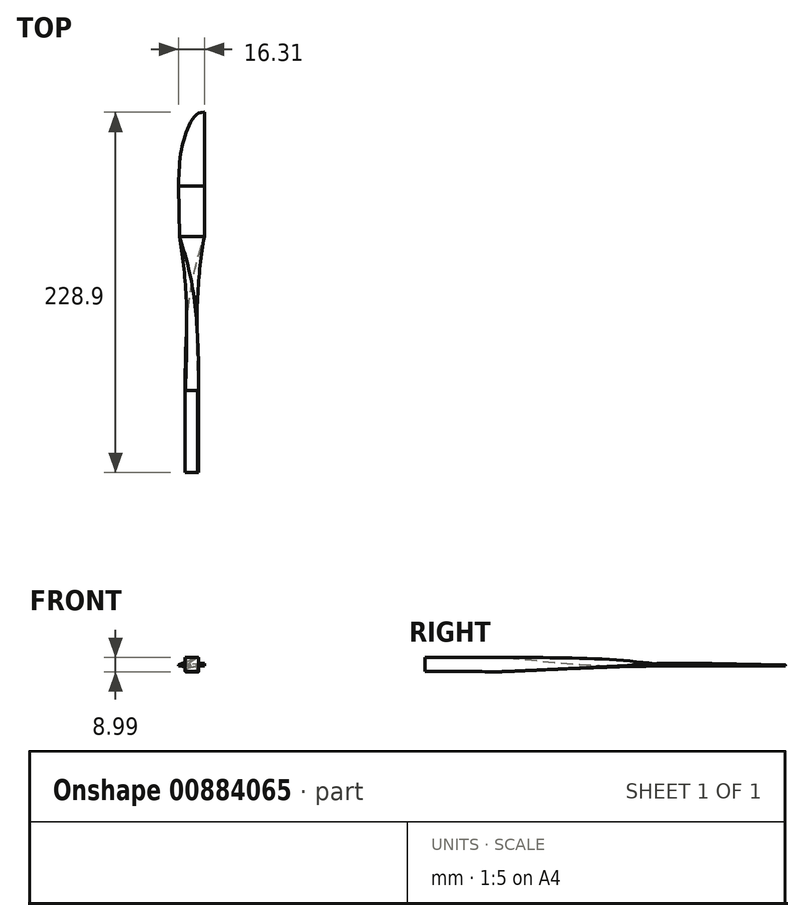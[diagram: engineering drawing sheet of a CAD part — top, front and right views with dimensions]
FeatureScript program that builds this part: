
annotation { "Feature Type Name" : "Feature", "Feature Type Description" : "" }
export const myFeature = defineFeature(function(context is Context, id is Id, definition is map)
    precondition{}
    {
        {
            var Q0;
            Q0=qCreatedBy(makeId("Front.planeOp"),FACE);
            var sketch = newSketch(context, id + "F0", { "sketchPlane" : qUnion([Q0])});
            skLineSegment(sketch, "E0.bottom", {"start": v(4.2, 4.4) * mm, "end": v(-4.2, 4.4) * mm});
            skLineSegment(sketch, "E0.top", {"start": v(4.2, -4.4) * mm, "end": v(-4.2, -4.4) * mm});
            skLineSegment(sketch, "E0.left", {"start": v(4.2, 4.4) * mm, "end": v(4.2, -4.4) * mm});
            skLineSegment(sketch, "E0.right", {"start": v(-4.2, 4.4) * mm, "end": v(-4.2, -4.4) * mm});
            skPoint(sketch, "E0.middle", {"position": v(0, 0) * mm});
            skSolve(sketch);
        }
        {
            var Q0;
            Q0=qCreatedBy(makeId("Front.planeOp"),FACE);
            cPlane(context, id + "F1", {"entities" : qUnion([Q0]), "cplaneType" : CPlaneType.OFFSET, "offset" : 120 * mm, "oppositeDirection" : true, "width" : 150 * mm, "height" : 150 * mm});
        }
        {
            var Q0;
            Q0=qCreatedBy(makeId("Front.planeOp"),FACE);
            cPlane(context, id + "F2", {"entities" : qUnion([Q0]), "cplaneType" : CPlaneType.OFFSET, "offset" : 52 * mm, "oppositeDirection" : true, "width" : 150 * mm, "height" : 150 * mm});
        }
        {
            var Q0;
            Q0=qCreatedBy(id+"F2.planeOp",FACE);
            var sketch = newSketch(context, id + "F3", { "sketchPlane" : qUnion([Q0])});
            skLineSegment(sketch, "E1.0.0", {"start": v(-4.2, -4.4) * mm, "end": v(4.2, -4.4) * mm});
            skLineSegment(sketch, "E1.0.1", {"start": v(4.2, -4.4) * mm, "end": v(4.2, 4.4) * mm});
            skLineSegment(sketch, "E1.0.2", {"start": v(4.2, 4.4) * mm, "end": v(-4.2, 4.4) * mm});
            skLineSegment(sketch, "E1.0.3", {"start": v(-4.2, 4.4) * mm, "end": v(-4.2, -4.4) * mm});
            skSolve(sketch);
        }
        {
            var Q0;
            Q0=sQuery(id+"F0.wireOp",VERTEX,"E0.bottom.end");
            var Q1;
            Q1=sQuery(id+"F3.wireOp",VERTEX,"E1.0.2.end");
            var Q2;
            Q2=sQuery(id+"F3.wireOp",VERTEX,"E1.0.1.end");
            cPlane(context, id + "F4", {"entities" : qUnion([Q0, Q1, Q2]), "cplaneType" : CPlaneType.THREE_POINT, "offset" : 25 * mm, "width" : 150 * mm, "height" : 150 * mm});
        }
        {
            var Q0;
            Q0=qCreatedBy(id+"F4.planeOp",FACE);
            var sketch = newSketch(context, id + "F5", { "sketchPlane" : qUnion([Q0])});
            skLineSegment(sketch, "E2", {"start": v(-12.8, 0) * mm, "end": v(-12.8, 52) * mm});
            skLineSegment(sketch, "E3", {"start": v(4.2, 0) * mm, "end": v(4.2, 52) * mm});
            skLineSegment(sketch, "E4.0", {"start": v(4.2, 52) * mm, "end": v(-12.8, 52) * mm});
            skLineSegment(sketch, "E5.0", {"start": v(4.2, 0) * mm, "end": v(-12.8, 0) * mm});
            skPoint(sketch, "E6.orphan", {"position": v(-4.2, 52) * mm});
            skPoint(sketch, "E7.orphan", {"position": v(-4.2, 0) * mm});
            skSolve(sketch);
        }
        {
            var Q0;
            Q0=qCreatedBy(id+"F1.planeOp",FACE);
            var sketch = newSketch(context, id + "F6", { "sketchPlane" : qUnion([Q0])});
            skLineSegment(sketch, "E8", {"start": v(-4.15, -1) * mm, "end": v(4.15, -1) * mm, "construction": true});
            skPoint(sketch, "E9", {"position": v(0, -1) * mm});
            skPoint(sketch, "E10", {"position": v(0, 3) * mm});
            skLineSegment(sketch, "E11", {"start": v(4.15, -1) * mm, "end": v(0, 3) * mm});
            skLineSegment(sketch, "E12", {"start": v(-4.15, -1) * mm, "end": v(0, 3) * mm});
            skLineSegment(sketch, "E13", {"start": v(-4.15, -1) * mm, "end": v(0, -1.5) * mm});
            skLineSegment(sketch, "E14", {"start": v(0, -1.5) * mm, "end": v(4.15, -1) * mm});
            skSolve(sketch);
        }
        {
            var Q0;
            Q0=qCreatedBy(id+"F1.planeOp",FACE);
            cPlane(context, id + "F7", {"entities" : qUnion([Q0]), "cplaneType" : CPlaneType.OFFSET, "offset" : 30 * mm, "oppositeDirection" : true, "width" : 150 * mm, "height" : 150 * mm});
        }
        {
            var Q0;
            Q0=qCreatedBy(id+"F7.planeOp",FACE);
            var sketch = newSketch(context, id + "F8", { "sketchPlane" : qUnion([Q0])});
            skLineSegment(sketch, "E15.bottom", {"start": v(-7.87, -0.75) * mm, "end": v(7.87, -0.75) * mm});
            skLineSegment(sketch, "E15.top", {"start": v(-7.88, 0.05) * mm, "end": v(7.87, 0.75) * mm});
            skLineSegment(sketch, "E15.left", {"start": v(-7.87, -0.75) * mm, "end": v(-7.87, 0.05) * mm});
            skLineSegment(sketch, "E15.right", {"start": v(7.87, -0.75) * mm, "end": v(7.87, 0.75) * mm});
            skPoint(sketch, "E16", {"position": v(0, -0.75) * mm});
            skSolve(sketch);
        }
        {
            var Q0;
            Q0=makeQuery(id+"F0.imprint","IMPRINT",FACE,{"disambiguationData":[TD([[makeQuery(id+"F0.imprint","IMPRINT",EDGE,{"derivedFrom":sQuery(id+"F0.wireOp",EDGE,"E0.bottom")}),1.0]])]});
            var Q1;
            Q1=makeQuery(id+"F3.imprint","IMPRINT",FACE,{"disambiguationData":[TD([[makeQuery(id+"F3.imprint","IMPRINT",EDGE,{"derivedFrom":sQuery(id+"F3.wireOp",EDGE,"E1.0.0")}),1.0]])]});
            var Q2;
            Q2 = qSketchRegion(id + "F6", true);
            var Q3;
            Q3 = qSketchRegion(id + "F8", true);
            var Q4;
            Q4=sQuery(id+"F5.wireOp",EDGE,"E2");
            var Q5;
            Q5=sQuery(id+"F5.wireOp",EDGE,"E3");
            var Q6;
            Q6=sQuery(id+"F0.wireOp",VERTEX,"E0.bottom.start");
            var Q7;
            Q7=sQuery(id+"F3.wireOp",VERTEX,"E1.0.1.end");
            var Q8;
            Q8=sQuery(id+"F6.wireOp",VERTEX,"E10");
            var Q9;
            Q9=sQuery(id+"F8.wireOp",VERTEX,"E15.top.start");
            loft(context, id + "F9", {"startCondition" : LoftEndDerivativeType.NORMAL_TO_PROFILE, "startMagnitude" : 2.75, "sheetProfilesArray" : [{ "sheetProfileEntities" : qUnion([Q0]) }, { "sheetProfileEntities" : qUnion([Q1]) }, { "sheetProfileEntities" : qUnion([Q2]) }, { "sheetProfileEntities" : qUnion([Q3]) }], "guidesArray" : [{ "guideEntities" : qUnion([Q4]), "guideDerivativeType" : LoftGuideDerivativeType.DEFAULT, "guideDerivativeMagnitude" : 1 }, { "guideEntities" : qUnion([Q5]), "guideDerivativeType" : LoftGuideDerivativeType.DEFAULT, "guideDerivativeMagnitude" : 1 }], "matchConnections" : true, "connections" : [{ "connectionEntities" : qUnion([Q6, Q7, Q8, Q9]), "connectionEdgeQueries" : qUnion([]), "connectionEdgeParameters" : [] }]});
        }
        {
            var Q0;
            Q0 = qSketchRegion(id + "F5", true);
            extrude(context, id + "F10", {"entities" : qUnion([Q0]), "operationType" : NewBodyOperationType.REMOVE, "endBound" : BoundingType.THROUGH_ALL, "depth" : 25 * mm, "offsetDistance" : 25 * mm});
        }
        {
            var Q0;
            Q0=qCreatedBy(id+"F7.planeOp",FACE);
            cPlane(context, id + "F11", {"entities" : qUnion([Q0]), "cplaneType" : CPlaneType.OFFSET, "offset" : 32 * mm, "oppositeDirection" : true, "width" : 150 * mm, "height" : 150 * mm});
        }
        {
            var Q0;
            Q0=qCreatedBy(id+"F11.planeOp",FACE);
            cPlane(context, id + "F12", {"entities" : qUnion([Q0]), "cplaneType" : CPlaneType.OFFSET, "offset" : 46.9 * mm, "oppositeDirection" : true, "width" : 150 * mm, "height" : 150 * mm});
        }
        {
            var Q0;
            Q0=qCreatedBy(id+"F11.planeOp",FACE);
            var sketch = newSketch(context, id + "F13", { "sketchPlane" : qUnion([Q0])});
            skLineSegment(sketch, "E17", {"start": v(7.87, -0.75) * mm, "end": v(-8.43, -0.75) * mm});
            skLineSegment(sketch, "E18", {"start": v(7.87, -0.75) * mm, "end": v(7.87, 0.65) * mm});
            skLineSegment(sketch, "E19", {"start": v(7.87, 0.65) * mm, "end": v(-8.43, -0.35) * mm});
            skLineSegment(sketch, "E20", {"start": v(-8.43, -0.35) * mm, "end": v(-8.43, -0.75) * mm});
            skPoint(sketch, "E21", {"position": v(7.87, -0.35) * mm});
            skSolve(sketch);
        }
        {
            var Q0;
            Q0=qCreatedBy(id+"F12.planeOp",FACE);
            var sketch = newSketch(context, id + "F14", { "sketchPlane" : qUnion([Q0])});
            skPoint(sketch, "E22", {"position": v(7.87, -0.75) * mm});
            skPoint(sketch, "E23", {"position": v(7.87, -0.35) * mm});
            skLineSegment(sketch, "E24", {"start": v(7.87, -0.35) * mm, "end": v(7.87, -0.75) * mm});
            skLineSegment(sketch, "E25", {"start": v(7.87, -0.35) * mm, "end": v(7.86, -0.35) * mm});
            skLineSegment(sketch, "E26", {"start": v(7.86, -0.35) * mm, "end": v(7.86, -0.75) * mm});
            skLineSegment(sketch, "E27", {"start": v(7.86, -0.75) * mm, "end": v(7.87, -0.75) * mm});
            skSolve(sketch);
        }
        {
            var Q0;
            Q0=sQuery(id+"F13.wireOp",VERTEX,"E17.start");
            var Q1;
            Q1=sQuery(id+"F13.wireOp",VERTEX,"E17.end");
            var Q2;
            Q2=sQuery(id+"F14.wireOp",VERTEX,"E22");
            cPlane(context, id + "F15", {"entities" : qUnion([Q0, Q1, Q2]), "cplaneType" : CPlaneType.THREE_POINT, "offset" : 25 * mm, "width" : 150 * mm, "height" : 150 * mm});
        }
        {
            var Q0;
            Q0=qCreatedBy(id+"F15.planeOp",FACE);
            var sketch = newSketch(context, id + "F16", { "sketchPlane" : qUnion([Q0])});
            skFitSpline(sketch, "E28", {"points": [v(-8.43, 182) * mm, v(-8.09, 191.61) * mm, v(-6.77, 204.38) * mm, v(-4.71, 212.76) * mm, v(-1.33, 221.62) * mm, v(2.94, 227.54) * mm, v(7.86, 228.9) * mm], "startDerivative": vector(0, 51.26) * mm, "endDerivative": vector(52.5, 0) * mm});
            skLineSegment(sketch, "E29", {"start": v(7.87, 182) * mm, "end": v(7.87, 228.9) * mm});
            skSolve(sketch);
        }
        {
            var Q1;
            Q1=makeQuery(id+"F8.imprint","IMPRINT",FACE,{"disambiguationData":[TD([[makeQuery(id+"F8.imprint","IMPRINT",EDGE,{"derivedFrom":sQuery(id+"F8.wireOp",EDGE,"E15.bottom")}),1.0]])]});
            var Q2;
            Q2=makeQuery(id+"F13.imprint","IMPRINT",FACE,{"disambiguationData":[TD([[makeQuery(id+"F13.imprint","IMPRINT",EDGE,{"derivedFrom":sQuery(id+"F13.wireOp",EDGE,"E17")}),-1.0]])]});
            loft(context, id + "F17", {"operationType" : NewBodyOperationType.ADD, "sheetProfilesArray" : [{ "sheetProfileEntities" : qUnion([Q1]) }, { "sheetProfileEntities" : qUnion([Q2]) }]});
        }
        {
            var Q0;
            Q0=sQuery(id+"F14.wireOp",VERTEX,"E25.end");
            var Q1;
            Q1=sQuery(id+"F13.wireOp",VERTEX,"E19.end");
            var Q2;
            Q2=sQuery(id+"F13.wireOp",VERTEX,"E21");
            cPlane(context, id + "F18", {"entities" : qUnion([Q0, Q1, Q2]), "cplaneType" : CPlaneType.THREE_POINT, "offset" : 25 * mm, "width" : 150 * mm, "height" : 150 * mm});
        }
        {
            var Q0;
            Q0=qCreatedBy(id+"F18.planeOp",FACE);
            var sketch = newSketch(context, id + "F19", { "sketchPlane" : qUnion([Q0])});
            skFitSpline(sketch, "E30", {"points": [v(-8.43, -182) * mm, v(-8.09, -191.61) * mm, v(-6.77, -204.38) * mm, v(-4.71, -212.76) * mm, v(-1.33, -221.62) * mm, v(2.94, -227.54) * mm, v(7.86, -228.9) * mm], "startDerivative": vector(0, -51.26) * mm, "endDerivative": vector(52.5, 0) * mm});
            skSolve(sketch);
        }
        {
            var Q0;
            Q0=sQuery(id+"F13.wireOp",VERTEX,"E18.end");
            var Q1;
            Q1=sQuery(id+"F13.wireOp",VERTEX,"E17.start");
            var Q2;
            Q2=sQuery(id+"F14.wireOp",VERTEX,"E23");
            cPlane(context, id + "F20", {"entities" : qUnion([Q0, Q1, Q2]), "cplaneType" : CPlaneType.THREE_POINT, "offset" : 25 * mm, "width" : 150 * mm, "height" : 150 * mm});
        }
        {
            var Q0;
            Q0=qCreatedBy(id+"F20.planeOp",FACE);
            var sketch = newSketch(context, id + "F21", { "sketchPlane" : qUnion([Q0])});
            skLineSegment(sketch, "E31", {"start": v(-182, 0.65) * mm, "end": v(-228.9, -0.35) * mm});
            skSolve(sketch);
        }
        {
            var Q0;
            Q0=sQuery(id+"F16.wireOp",EDGE,"E28");
            var Q1;
            Q1=sQuery(id+"F16.wireOp",EDGE,"5XTyuvPo-rvK6-CgZZ-tZF8-A382pJMBjB2j");
            var Q3;
            Q3=makeQuery(id+"F14.imprint","IMPRINT",FACE,{"disambiguationData":[TD([[makeQuery(id+"F14.imprint","IMPRINT",EDGE,{"derivedFrom":sQuery(id+"F14.wireOp",EDGE,"E24")}),-1.0]])]});
            var Q4;
            Q4=makeQuery(id+"F13.imprint","IMPRINT",FACE,{"disambiguationData":[TD([[makeQuery(id+"F13.imprint","IMPRINT",EDGE,{"derivedFrom":sQuery(id+"F13.wireOp",EDGE,"E17")}),-1.0]])]});
            var Q5;
            Q5=sQuery(id+"F16.wireOp",EDGE,"E28");
            var Q6;
            Q6=sQuery(id+"F16.wireOp",EDGE,"5XTyuvPo-rvK6-CgZZ-tZF8-A382pJMBjB2j");
            var Q7;
            Q7=sQuery(id+"F19.wireOp",EDGE,"E30");
            var Q8;
            Q8=sQuery(id+"F21.wireOp",EDGE,"E31");
            loft(context, id + "F22", {"operationType" : NewBodyOperationType.ADD, "spine" : qUnion([Q0, Q1]), "addGuides" : true, "sheetProfilesArray" : [{ "sheetProfileEntities" : qUnion([Q3]) }, { "sheetProfileEntities" : qUnion([Q4]) }], "guidesArray" : [{ "guideEntities" : qUnion([Q5]), "guideDerivativeType" : LoftGuideDerivativeType.DEFAULT, "guideDerivativeMagnitude" : 1 }, { "guideEntities" : qUnion([Q6]), "guideDerivativeType" : LoftGuideDerivativeType.DEFAULT, "guideDerivativeMagnitude" : 1 }, { "guideEntities" : qUnion([Q7]), "guideDerivativeType" : LoftGuideDerivativeType.DEFAULT, "guideDerivativeMagnitude" : 1 }, { "guideEntities" : qUnion([Q8]), "guideDerivativeType" : LoftGuideDerivativeType.DEFAULT, "guideDerivativeMagnitude" : 1 }]});
        }
        {
            var Q0;
            Q0=makeQuery(id+"F9.opLoft","MID_CAP_EDGE",EDGE,{"disambiguationData":[OSD([sQuery(id+"F0.wireOp",EDGE,"E0.bottom"),sQuery(id+"F0.wireOp",EDGE,"E0.top"),sQuery(id+"F0.wireOp",EDGE,"E0.left")])],"capPos":0.0});
            cPlane(context, id + "F23", {"entities" : qUnion([Q0]), "cplaneType" : CPlaneType.LINE_ANGLE, "offset" : 25 * mm, "angle" : 55 * degree, "width" : 150 * mm, "height" : 150 * mm});
        }
    });
